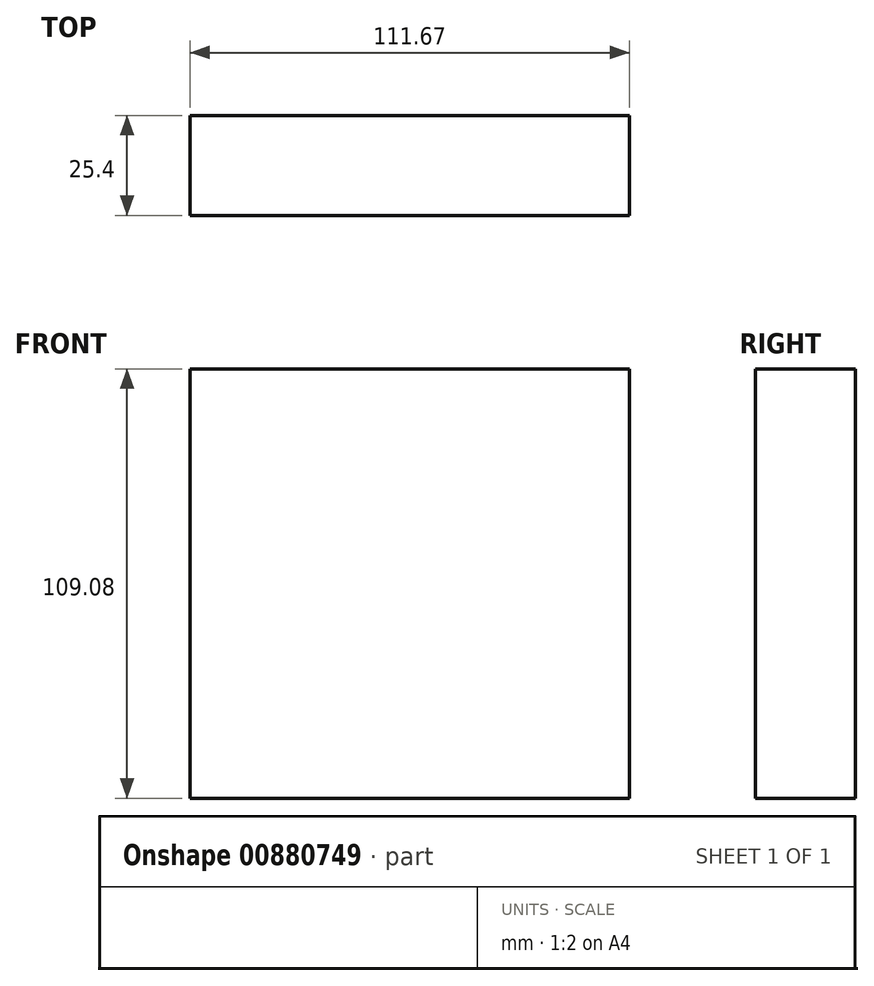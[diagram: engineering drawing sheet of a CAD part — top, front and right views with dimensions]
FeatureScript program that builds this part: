
annotation { "Feature Type Name" : "Feature", "Feature Type Description" : "" }
export const myFeature = defineFeature(function(context is Context, id is Id, definition is map)
    precondition{}
    {
        {
            var Q0;
            Q0=qCreatedBy(makeId("Front.planeOp"),FACE);
            var sketch = newSketch(context, id + "F0", { "sketchPlane" : qUnion([Q0])});
            skLineSegment(sketch, "E0.bottom", {"start": v(-60.3, 54.25) * mm, "end": v(51.37, 54.25) * mm});
            skLineSegment(sketch, "E0.top", {"start": v(-60.3, -54.83) * mm, "end": v(51.37, -54.83) * mm});
            skLineSegment(sketch, "E0.left", {"start": v(-60.3, 54.25) * mm, "end": v(-60.3, -54.83) * mm});
            skLineSegment(sketch, "E0.right", {"start": v(51.37, 54.25) * mm, "end": v(51.37, -54.83) * mm});
            skSolve(sketch);
        }
        {
            var Q0;
            Q0=makeQuery(id+"F0.imprint","IMPRINT",FACE,{"disambiguationData":[TD([[makeQuery(id+"F0.imprint","IMPRINT",EDGE,{"derivedFrom":sQuery(id+"F0.wireOp",EDGE,"E0.bottom")}),-1.0]])]});
            extrude(context, id + "F1", {"entities" : qUnion([Q0]), "depth" : 25.4 * mm, "offsetDistance" : 25.4 * mm});
        }
    });
